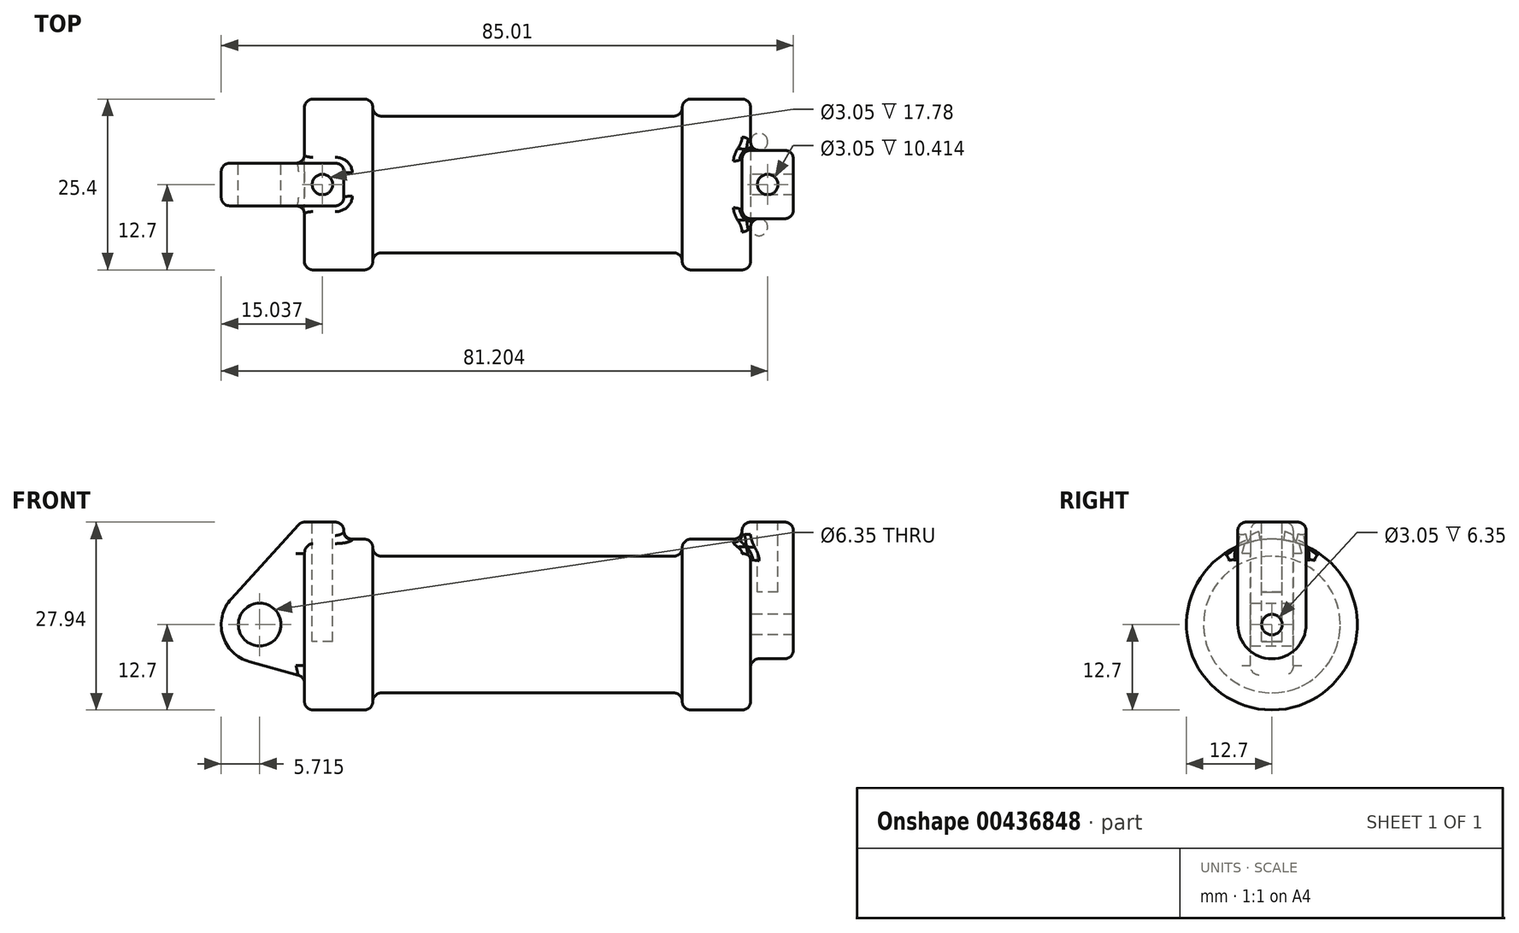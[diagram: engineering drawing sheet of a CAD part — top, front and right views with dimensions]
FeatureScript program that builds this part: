
annotation { "Feature Type Name" : "Feature", "Feature Type Description" : "" }
export const myFeature = defineFeature(function(context is Context, id is Id, definition is map)
    precondition{}
    {
        {
            var Q0;
            Q0=qCreatedBy(makeId("Front.planeOp"),FACE);
            var sketch = newSketch(context, id + "F0", { "sketchPlane" : qUnion([Q0])});
            skLineSegment(sketch, "E0", {"start": v(0, 0) * mm, "end": v(0, 12.7) * mm});
            skLineSegment(sketch, "E1", {"start": v(0, 12.7) * mm, "end": v(10.16, 12.7) * mm});
            skLineSegment(sketch, "E2", {"start": v(10.16, 12.7) * mm, "end": v(10.16, 10.16) * mm});
            skLineSegment(sketch, "E3", {"start": v(10.16, 10.16) * mm, "end": v(56.13, 10.16) * mm});
            skLineSegment(sketch, "E4", {"start": v(56.13, 10.16) * mm, "end": v(56.13, 12.7) * mm});
            skLineSegment(sketch, "E5", {"start": v(56.13, 12.7) * mm, "end": v(66.3, 12.7) * mm});
            skLineSegment(sketch, "E6", {"start": v(66.3, 12.7) * mm, "end": v(66.3, 0) * mm});
            skLineSegment(sketch, "E7", {"start": v(66.3, 0) * mm, "end": v(0, 0) * mm});
            skLineSegment(sketch, "E8", {"start": v(5.84, 15.24) * mm, "end": v(-0.5, 15.24) * mm});
            skLineSegment(sketch, "E9", {"start": v(-0.5, 15.24) * mm, "end": v(-10.88, 3.85) * mm});
            skLineSegment(sketch, "E10", {"start": v(0, 0) * mm, "end": v(-6.65, 0) * mm});
            skCircle(sketch, "E11", {"center": v(-6.65, 0) * mm, "radius": 5.72 * mm});
            skCircle(sketch, "E12", {"center": v(-6.65, 0) * mm, "radius": 3.18 * mm});
            skLineSegment(sketch, "E13", {"start": v(5.84, 15.24) * mm, "end": v(5.84, -9.4) * mm});
            skLineSegment(sketch, "E14", {"start": v(5.84, -9.4) * mm, "end": v(-8.18, -5.5) * mm});
            skLineSegment(sketch, "E15", {"start": v(0, 0) * mm, "end": v(0, -7.78) * mm});
            skSolve(sketch);
        }
        {
            var Q0;
            {var subQ1=sQuery(id+"F0.wireOp",EDGE,"E0");Q0=makeQuery(id+"F0.imprint","IMPRINT",FACE,{"disambiguationData":[TD([[makeQuery(id+"F0.imprint","IMPRINT",EDGE,{"derivedFrom":subQ1}),1.0]])]});}
            var Q1;
            {var subQ5=sQuery(id+"F0.wireOp",EDGE,"E12");Q1=makeQuery(id+"F0.imprint","IMPRINT",FACE,{"disambiguationData":[TD([[makeQuery(id+"F0.imprint","IMPRINT",EDGE,{"derivedFrom":subQ5}),-1.0]])]});}
            var Q2;
            {var subQ0=sQuery(id+"F0.wireOp",EDGE,"E15");Q2=makeQuery(id+"F0.imprint","IMPRINT",FACE,{"disambiguationData":[TD([[makeQuery(id+"F0.imprint","IMPRINT",EDGE,{"derivedFrom":subQ0}),-1.0]])]});}
            var Q3;
            {var subQ0=sQuery(id+"F0.wireOp",EDGE,"E0");Q3=makeQuery(id+"F0.imprint","IMPRINT",FACE,{"disambiguationData":[TD([[makeQuery(id+"F0.imprint","IMPRINT",EDGE,{"derivedFrom":subQ0}),-1.0]])]});}
            var Q4;
            {var subQ0=sQuery(id+"F0.wireOp",EDGE,"E15");Q4=makeQuery(id+"F0.imprint","IMPRINT",FACE,{"disambiguationData":[TD([[makeQuery(id+"F0.imprint","IMPRINT",EDGE,{"derivedFrom":subQ0}),1.0]])]});}
            extrude(context, id + "F1", {"entities" : qUnion([Q0, Q1, Q2, Q3, Q4]), "depth" : 3.17 * mm, "hasSecondDirection" : true, "secondDirectionOppositeDirection" : true, "secondDirectionDepth" : 3.17 * mm});
        }
        {
            var Q0;
            {var subQ0=sQuery(id+"F0.wireOp",EDGE,"E2");Q0=makeQuery(id+"F0.imprint","IMPRINT",FACE,{"disambiguationData":[TD([[makeQuery(id+"F0.imprint","IMPRINT",EDGE,{"derivedFrom":subQ0}),-1.0]])]});}
            var Q1;
            {var subQ0=sQuery(id+"F0.wireOp",EDGE,"E0");Q1=makeQuery(id+"F0.imprint","IMPRINT",FACE,{"disambiguationData":[TD([[makeQuery(id+"F0.imprint","IMPRINT",EDGE,{"derivedFrom":subQ0}),-1.0]])]});}
            var Q2;
            Q2=sQuery(id+"F0.wireOp",EDGE,"E7");
            revolve(context, id + "F2", {"operationType" : NewBodyOperationType.ADD, "entities" : qUnion([Q0, Q1]), "axis" : qUnion([Q2]), "revolveType" : RevolveType.FULL});
        }
        {
            var Q0;
            Q0=makeQuery(id+"F2.opRevolve","SWEPT_FACE",FACE,{"disambiguationData":[OSD([sQuery(id+"F0.wireOp",EDGE,"E6")])]});
            var sketch = newSketch(context, id + "F3", { "sketchPlane" : qUnion([Q0])});
            skCircle(sketch, "E16", {"center": v(0, 0) * mm, "radius": 1.52 * mm});
            skCircle(sketch, "E17", {"center": v(0, 0) * mm, "radius": 5.08 * mm});
            skLineSegment(sketch, "E18.top", {"start": v(5.08, 15.24) * mm, "end": v(-5.08, 15.24) * mm});
            skLineSegment(sketch, "E18.left", {"start": v(5.08, 0) * mm, "end": v(5.08, 15.24) * mm});
            skLineSegment(sketch, "E18.right", {"start": v(-5.08, 0) * mm, "end": v(-5.08, 15.24) * mm});
            skSolve(sketch);
        }
        {
            var Q0;
            Q0 = qSketchRegion(id + "F3", true);
            extrude(context, id + "F4", {"entities" : qUnion([Q0]), "operationType" : NewBodyOperationType.ADD, "depth" : 6.35 * mm, "hasSecondDirection" : true, "secondDirectionOppositeDirection" : true, "secondDirectionDepth" : 1.27 * mm});
        }
        {
            var Q0;
            Q0=makeQuery(id+"F1.opExtrude","SWEPT_FACE",FACE,{"disambiguationData":[OSD([sQuery(id+"F0.wireOp",EDGE,"E8")])]});
            var sketch = newSketch(context, id + "F5", { "sketchPlane" : qUnion([Q0])});
            skCircle(sketch, "E19", {"center": v(2.67, 0) * mm, "radius": 1.52 * mm});
            skPoint(sketch, "E19.centerSnap0", {"position": v(2.67, -3.18) * mm});
            skPoint(sketch, "E19.centerSnap1", {"position": v(5.84, 0) * mm});
            skSolve(sketch);
        }
        {
            var Q0;
            Q0 = qSketchRegion(id + "F5", true);
            extrude(context, id + "F6", {"entities" : qUnion([Q0]), "operationType" : NewBodyOperationType.REMOVE, "oppositeDirection" : true, "depth" : 17.78 * mm});
        }
        {
            var Q0;
            Q0=makeQuery(id+"F4.opExtrude","SWEPT_FACE",FACE,{"disambiguationData":[OSD([sQuery(id+"F3.wireOp",EDGE,"E18.top")])]});
            var sketch = newSketch(context, id + "F7", { "sketchPlane" : qUnion([Q0])});
            skCircle(sketch, "E20", {"center": v(68.83, 0) * mm, "radius": 1.52 * mm});
            skPoint(sketch, "E20.centerSnap0", {"position": v(65.02, 0) * mm});
            skPoint(sketch, "E20.centerSnap1", {"position": v(68.83, 5.08) * mm});
            skSolve(sketch);
        }
        {
            var Q0;
            Q0 = qSketchRegion(id + "F7", true);
            extrude(context, id + "F8", {"entities" : qUnion([Q0]), "operationType" : NewBodyOperationType.REMOVE, "oppositeDirection" : true, "depth" : 10.4 * mm});
        }
        {
            var Q0;
            Q0=makeQuery(id+"F2.opRevolve","SWEPT_EDGE",EDGE,{"disambiguationData":[OSD([sQuery(id+"F0.wireOp",EDGE,"E5"),sQuery(id+"F0.wireOp",EDGE,"E6")])]});
            var Q1;
            Q1=makeQuery(id+"F4.opExtrude","CAP_EDGE",EDGE,{"disambiguationData":[OSD([sQuery(id+"F3.wireOp",EDGE,"E18.right")])],"isStart":false});
            var Q2;
            Q2=makeQuery(id+"F4.opExtrude","CAP_EDGE",EDGE,{"disambiguationData":[OSD([sQuery(id+"F3.wireOp",EDGE,"E18.left")])],"isStart":false});
            var Q3;
            Q3=makeQuery(id+"F4.opExtrude","CAP_EDGE",EDGE,{"disambiguationData":[OSD([sQuery(id+"F3.wireOp",EDGE,"E17")])],"isStart":false});
            var Q4;
            Q4=makeQuery(id+"F4.opExtrude","SWEPT_EDGE",EDGE,{"disambiguationData":[OSD([sQuery(id+"F3.wireOp",EDGE,"E18.top"),sQuery(id+"F3.wireOp",EDGE,"E18.right")])]});
            var Q5;
            Q5=makeQuery(id+"F4.opExtrude","CAP_EDGE",EDGE,{"disambiguationData":[OSD([sQuery(id+"F3.wireOp",EDGE,"E18.top")])],"isStart":false});
            var Q6;
            Q6=makeQuery(id+"F4.opExtrude","SWEPT_EDGE",EDGE,{"disambiguationData":[OSD([sQuery(id+"F3.wireOp",EDGE,"E18.top"),sQuery(id+"F3.wireOp",EDGE,"E18.left")])]});
            var Q7;
            Q7=makeQuery(id+"F4.opExtrude","CAP_EDGE",EDGE,{"disambiguationData":[OSD([sQuery(id+"F3.wireOp",EDGE,"E18.top")])],"isStart":true});
            var Q8;
            Q8=makeQuery(id+"F4.opExtrude","CAP_EDGE",EDGE,{"disambiguationData":[OSD([sQuery(id+"F3.wireOp",EDGE,"E18.right")])],"isStart":true});
            var Q9;
            Q9=makeQuery(id+"F4.opExtrude","CAP_EDGE",EDGE,{"disambiguationData":[OSD([sQuery(id+"F3.wireOp",EDGE,"E18.left")])],"isStart":true});
            var Q10;
            Q10=makeQuery(id+"F4.boolean.opBoolean","INTERSECT",EDGE,{"derivedFrom":[makeQuery(id+"F2.opRevolve","SWEPT_FACE",FACE,{"disambiguationData":[OSD([sQuery(id+"F0.wireOp",EDGE,"E5")])]}),makeQuery(id+"F4.opExtrude","SWEPT_FACE",FACE,{"disambiguationData":[OSD([sQuery(id+"F3.wireOp",EDGE,"E18.left")])]})]});
            var Q11;
            Q11=makeQuery(id+"F4.boolean.opBoolean","INTERSECT",EDGE,{"derivedFrom":[makeQuery(id+"F2.opRevolve","SWEPT_FACE",FACE,{"disambiguationData":[OSD([sQuery(id+"F0.wireOp",EDGE,"E6")])]}),makeQuery(id+"F4.opExtrude","SWEPT_FACE",FACE,{"disambiguationData":[OSD([sQuery(id+"F3.wireOp",EDGE,"E18.left")])]})]});
            var Q12;
            Q12=makeQuery(id+"F4.boolean.opBoolean","INTERSECT",EDGE,{"derivedFrom":[makeQuery(id+"F2.opRevolve","SWEPT_FACE",FACE,{"disambiguationData":[OSD([sQuery(id+"F0.wireOp",EDGE,"E5")])]}),makeQuery(id+"F4.opExtrude","SWEPT_FACE",FACE,{"disambiguationData":[OSD([sQuery(id+"F3.wireOp",EDGE,"E18.right")])]})]});
            var Q13;
            Q13=makeQuery(id+"F4.boolean.opBoolean","INTERSECT",EDGE,{"derivedFrom":[makeQuery(id+"F2.opRevolve","SWEPT_FACE",FACE,{"disambiguationData":[OSD([sQuery(id+"F0.wireOp",EDGE,"E6")])]}),makeQuery(id+"F4.opExtrude","SWEPT_FACE",FACE,{"disambiguationData":[OSD([sQuery(id+"F3.wireOp",EDGE,"E18.right")])]})]});
            var Q14;
            Q14=makeQuery(id+"F4.opExtrude","SWEPT_FACE",FACE,{"disambiguationData":[OSD([sQuery(id+"F3.wireOp",EDGE,"E18.right")])]});
            var Q15;
            Q15=makeQuery(id+"F4.boolean.opBoolean","INTERSECT",EDGE,{"derivedFrom":[makeQuery(id+"F2.opRevolve","SWEPT_FACE",FACE,{"disambiguationData":[OSD([sQuery(id+"F0.wireOp",EDGE,"E5")])]}),makeQuery(id+"F4.opExtrude","CAP_FACE",FACE,{"disambiguationData":[OSD([sQuery(id+"F3.wireOp",EDGE,"E16"),sQuery(id+"F3.wireOp",EDGE,"E17"),sQuery(id+"F3.wireOp",EDGE,"E18.top"),sQuery(id+"F3.wireOp",EDGE,"E18.left"),sQuery(id+"F3.wireOp",EDGE,"E18.right")])],"isStart":true})]});
            var Q16;
            Q16=makeQuery(id+"F2.opRevolve","SWEPT_EDGE",EDGE,{"disambiguationData":[OSD([sQuery(id+"F0.wireOp",EDGE,"E4"),sQuery(id+"F0.wireOp",EDGE,"E5")])]});
            var Q17;
            Q17=makeQuery(id+"F2.opRevolve","SWEPT_EDGE",EDGE,{"disambiguationData":[OSD([sQuery(id+"F0.wireOp",EDGE,"E3"),sQuery(id+"F0.wireOp",EDGE,"E4")])]});
            var Q18;
            Q18=makeQuery(id+"F1.opExtrude","CAP_EDGE",EDGE,{"disambiguationData":[OSD([sQuery(id+"F0.wireOp",EDGE,"E8")])],"isStart":false});
            var Q19;
            Q19=makeQuery(id+"F1.opExtrude","CAP_EDGE",EDGE,{"disambiguationData":[OSD([sQuery(id+"F0.wireOp",EDGE,"E9")])],"isStart":false});
            var Q20;
            Q20=makeQuery(id+"F1.opExtrude","SWEPT_EDGE",EDGE,{"disambiguationData":[OSD([sQuery(id+"F0.wireOp",EDGE,"E8"),sQuery(id+"F0.wireOp",EDGE,"E9")])]});
            var Q21;
            Q21=makeQuery(id+"F1.opExtrude","CAP_EDGE",EDGE,{"disambiguationData":[OSD([sQuery(id+"F0.wireOp",EDGE,"E8")])],"isStart":true});
            var Q22;
            Q22=makeQuery(id+"F1.opExtrude","SWEPT_EDGE",EDGE,{"disambiguationData":[OSD([sQuery(id+"F0.wireOp",EDGE,"E8"),sQuery(id+"F0.wireOp",EDGE,"E13")])]});
            var Q23;
            Q23=makeQuery(id+"F1.opExtrude","CAP_EDGE",EDGE,{"disambiguationData":[OSD([sQuery(id+"F0.wireOp",EDGE,"E9")])],"isStart":true});
            var Q24;
            Q24=makeQuery(id+"F2.boolean.opBoolean","INTERSECT",EDGE,{"derivedFrom":[makeQuery(id+"F1.opExtrude","CAP_FACE",FACE,{"disambiguationData":[OSD([sQuery(id+"F0.wireOp",EDGE,"E8"),sQuery(id+"F0.wireOp",EDGE,"E9"),sQuery(id+"F0.wireOp",EDGE,"E11"),sQuery(id+"F0.wireOp",EDGE,"E12"),sQuery(id+"F0.wireOp",EDGE,"E13"),sQuery(id+"F0.wireOp",EDGE,"E14")])],"isStart":false}),makeQuery(id+"F2.opRevolve","SWEPT_FACE",FACE,{"disambiguationData":[OSD([sQuery(id+"F0.wireOp",EDGE,"E0")])]})]});
            var Q25;
            Q25=makeQuery(id+"F2.boolean.opBoolean","INTERSECT",EDGE,{"derivedFrom":[makeQuery(id+"F1.opExtrude","CAP_FACE",FACE,{"disambiguationData":[OSD([sQuery(id+"F0.wireOp",EDGE,"E8"),sQuery(id+"F0.wireOp",EDGE,"E9"),sQuery(id+"F0.wireOp",EDGE,"E11"),sQuery(id+"F0.wireOp",EDGE,"E12"),sQuery(id+"F0.wireOp",EDGE,"E13"),sQuery(id+"F0.wireOp",EDGE,"E14")])],"isStart":false}),makeQuery(id+"F2.opRevolve","SWEPT_FACE",FACE,{"disambiguationData":[OSD([sQuery(id+"F0.wireOp",EDGE,"E1")])]})]});
            var Q26;
            Q26=makeQuery(id+"F1.opExtrude","CAP_EDGE",EDGE,{"disambiguationData":[OSD([sQuery(id+"F0.wireOp",EDGE,"E13")])],"isStart":false});
            var Q27;
            Q27=makeQuery(id+"F1.opExtrude","CAP_EDGE",EDGE,{"disambiguationData":[OSD([sQuery(id+"F0.wireOp",EDGE,"E11")])],"isStart":false});
            var Q28;
            Q28=makeQuery(id+"F1.opExtrude","CAP_EDGE",EDGE,{"disambiguationData":[OSD([sQuery(id+"F0.wireOp",EDGE,"E11")])],"isStart":true});
            var Q29;
            Q29=makeQuery(id+"F1.opExtrude","CAP_EDGE",EDGE,{"disambiguationData":[OSD([sQuery(id+"F0.wireOp",EDGE,"E14")])],"isStart":false});
            var Q30;
            Q30=makeQuery(id+"F2.opRevolve","SWEPT_EDGE",EDGE,{"disambiguationData":[OSD([sQuery(id+"F0.wireOp",EDGE,"E0"),sQuery(id+"F0.wireOp",EDGE,"E1")])]});
            var Q31;
            Q31=makeQuery(id+"F2.opRevolve","SWEPT_EDGE",EDGE,{"disambiguationData":[OSD([sQuery(id+"F0.wireOp",EDGE,"E1"),sQuery(id+"F0.wireOp",EDGE,"E2")])]});
            var Q32;
            Q32=makeQuery(id+"F2.opRevolve","SWEPT_EDGE",EDGE,{"disambiguationData":[OSD([sQuery(id+"F0.wireOp",EDGE,"E2"),sQuery(id+"F0.wireOp",EDGE,"E3")])]});
            var Q33;
            Q33=makeQuery(id+"F2.boolean.opBoolean","INTERSECT",EDGE,{"derivedFrom":[makeQuery(id+"F1.opExtrude","SWEPT_FACE",FACE,{"disambiguationData":[OSD([sQuery(id+"F0.wireOp",EDGE,"E13")])]}),makeQuery(id+"F2.opRevolve","SWEPT_FACE",FACE,{"disambiguationData":[OSD([sQuery(id+"F0.wireOp",EDGE,"E1")])]})]});
            var Q34;
            Q34=makeQuery(id+"F1.opExtrude","CAP_EDGE",EDGE,{"disambiguationData":[OSD([sQuery(id+"F0.wireOp",EDGE,"E13")])],"isStart":true});
            var Q35;
            Q35=makeQuery(id+"F1.opExtrude","CAP_EDGE",EDGE,{"disambiguationData":[OSD([sQuery(id+"F0.wireOp",EDGE,"E14")])],"isStart":true});
            var Q36;
            Q36=makeQuery(id+"F2.boolean.opBoolean","INTERSECT",EDGE,{"derivedFrom":[makeQuery(id+"F1.opExtrude","CAP_FACE",FACE,{"disambiguationData":[OSD([sQuery(id+"F0.wireOp",EDGE,"E8"),sQuery(id+"F0.wireOp",EDGE,"E9"),sQuery(id+"F0.wireOp",EDGE,"E11"),sQuery(id+"F0.wireOp",EDGE,"E12"),sQuery(id+"F0.wireOp",EDGE,"E13"),sQuery(id+"F0.wireOp",EDGE,"E14")])],"isStart":true}),makeQuery(id+"F2.opRevolve","SWEPT_FACE",FACE,{"disambiguationData":[OSD([sQuery(id+"F0.wireOp",EDGE,"E0")])]})]});
            var Q37;
            Q37=makeQuery(id+"F2.opRevolve","SWEPT_FACE",FACE,{"disambiguationData":[OSD([sQuery(id+"F0.wireOp",EDGE,"E3")])]});
            var Q38;
            Q38=makeQuery(id+"F2.boolean.opBoolean","INTERSECT",EDGE,{"derivedFrom":[makeQuery(id+"F1.opExtrude","CAP_FACE",FACE,{"disambiguationData":[OSD([sQuery(id+"F0.wireOp",EDGE,"E8"),sQuery(id+"F0.wireOp",EDGE,"E9"),sQuery(id+"F0.wireOp",EDGE,"E11"),sQuery(id+"F0.wireOp",EDGE,"E12"),sQuery(id+"F0.wireOp",EDGE,"E13"),sQuery(id+"F0.wireOp",EDGE,"E14")])],"isStart":true}),makeQuery(id+"F2.opRevolve","SWEPT_FACE",FACE,{"disambiguationData":[OSD([sQuery(id+"F0.wireOp",EDGE,"E1")])]})]});
            var Q39;
            Q39=makeQuery(id+"F2.boolean.opBoolean","INTERSECT",EDGE,{"derivedFrom":[makeQuery(id+"F1.opExtrude","SWEPT_FACE",FACE,{"disambiguationData":[OSD([sQuery(id+"F0.wireOp",EDGE,"E14")])]}),makeQuery(id+"F2.opRevolve","SWEPT_FACE",FACE,{"disambiguationData":[OSD([sQuery(id+"F0.wireOp",EDGE,"E0")])]})]});
            var Q40;
            Q40=makeQuery(id+"F4.boolean.opBoolean","INTERSECT",EDGE,{"derivedFrom":[makeQuery(id+"F2.opRevolve","SWEPT_FACE",FACE,{"disambiguationData":[OSD([sQuery(id+"F0.wireOp",EDGE,"E6")])]}),makeQuery(id+"F4.opExtrude","SWEPT_FACE",FACE,{"disambiguationData":[OSD([sQuery(id+"F3.wireOp",EDGE,"E17")])]})]});
            fillet(context, id + "F9", {"entities" : qUnion([Q0, Q1, Q2, Q3, Q4, Q5, Q6, Q7, Q8, Q9, Q10, Q11, Q12, Q13, Q14, Q15, Q16, Q17, Q18, Q19, Q20, Q21, Q22, Q23, Q24, Q25, Q26, Q27, Q28, Q29, Q30, Q31, Q32, Q33, Q34, Q35, Q36, Q37, Q38, Q39, Q40]), "radius" : 1.27 * mm, "tangentPropagation" : true, "allowEdgeOverflow" : false});
        }
    });
